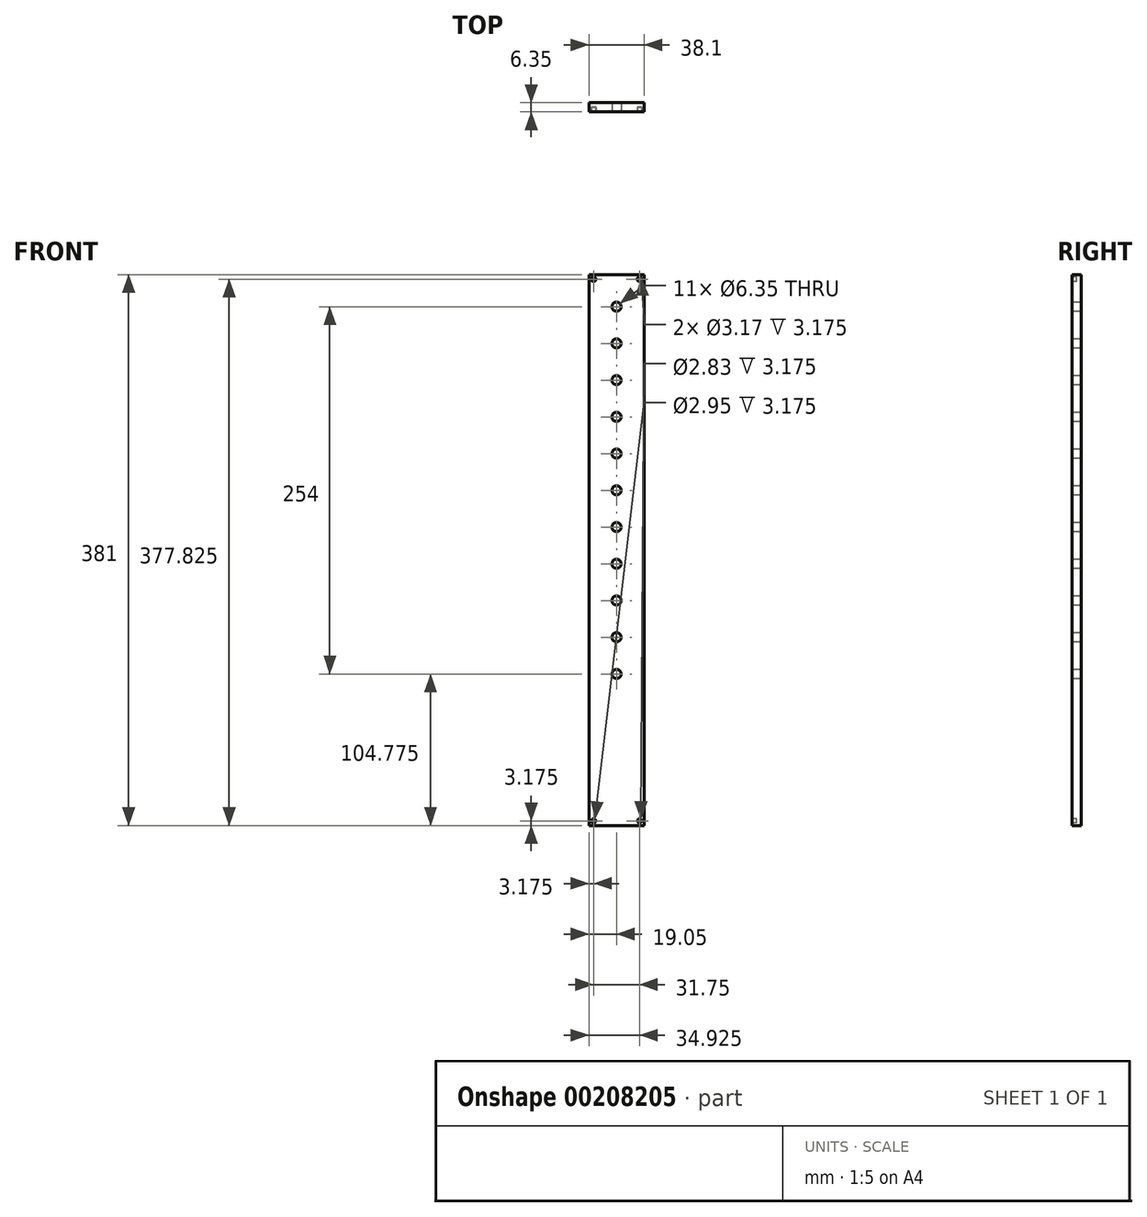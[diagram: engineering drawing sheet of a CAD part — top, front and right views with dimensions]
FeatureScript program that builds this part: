
annotation { "Feature Type Name" : "Feature", "Feature Type Description" : "" }
export const myFeature = defineFeature(function(context is Context, id is Id, definition is map)
    precondition{}
    {
        {
            var Q0;
            Q0=qCreatedBy(makeId("Front.planeOp"),FACE);
            var sketch = newSketch(context, id + "F0", { "sketchPlane" : qUnion([Q0])});
            skLineSegment(sketch, "E0.bottom", {"start": v(-19.05, 190.5) * mm, "end": v(19.05, 190.5) * mm});
            skLineSegment(sketch, "E0.top", {"start": v(-19.05, -190.5) * mm, "end": v(19.05, -190.5) * mm});
            skLineSegment(sketch, "E0.left", {"start": v(-19.05, 190.5) * mm, "end": v(-19.05, -190.5) * mm});
            skLineSegment(sketch, "E0.right", {"start": v(19.05, 190.5) * mm, "end": v(19.05, -190.5) * mm});
            skPoint(sketch, "E0.middle", {"position": v(0, 0) * mm});
            skSolve(sketch);
        }
        {
            var Q0;
            Q0 = qSketchRegion(id + "F0", true);
            extrude(context, id + "F1", {"entities" : qUnion([Q0]), "depth" : 6.35 * mm});
        }
        {
            var Q0;
            Q0=makeQuery(id+"F1.opExtrude","CAP_FACE",FACE,{"disambiguationData":[OSD([sQuery(id+"F0.wireOp",EDGE,"E0.bottom"),sQuery(id+"F0.wireOp",EDGE,"E0.top"),sQuery(id+"F0.wireOp",EDGE,"E0.left"),sQuery(id+"F0.wireOp",EDGE,"E0.right")])],"isStart":false});
            var sketch = newSketch(context, id + "F2", { "sketchPlane" : qUnion([Q0])});
            skLineSegment(sketch, "E1", {"start": v(0, -190.5) * mm, "end": v(0, -88.9) * mm, "construction": true});
            skPoint(sketch, "E1.endSnap0", {"position": v(0, -190.5) * mm});
            skLineSegment(sketch, "E2", {"start": v(0, -88.9) * mm, "end": v(0, -82.55) * mm, "construction": true});
            skCircle(sketch, "E3", {"center": v(0, -85.73) * mm, "radius": 3.18 * mm});
            skLineSegment(sketch, "E4", {"start": v(0, -85.73) * mm, "end": v(0, -60.33) * mm, "construction": true});
            skLineSegment(sketch, "E5", {"start": v(0, -60.33) * mm, "end": v(0, -34.93) * mm, "construction": true});
            skLineSegment(sketch, "E6", {"start": v(0, -34.93) * mm, "end": v(0, -9.53) * mm, "construction": true});
            skLineSegment(sketch, "E7", {"start": v(0, -9.53) * mm, "end": v(0, 15.87) * mm, "construction": true});
            skLineSegment(sketch, "E8", {"start": v(0, 15.87) * mm, "end": v(0, 41.27) * mm, "construction": true});
            skLineSegment(sketch, "E9", {"start": v(0, 41.27) * mm, "end": v(0, 66.67) * mm, "construction": true});
            skLineSegment(sketch, "E10", {"start": v(0, 66.67) * mm, "end": v(0, 92.08) * mm, "construction": true});
            skLineSegment(sketch, "E11", {"start": v(0, 92.08) * mm, "end": v(0, 117.48) * mm, "construction": true});
            skLineSegment(sketch, "E12", {"start": v(0, 117.48) * mm, "end": v(0, 142.88) * mm, "construction": true});
            skLineSegment(sketch, "E13", {"start": v(0, 142.88) * mm, "end": v(0, 168.28) * mm, "construction": true});
            skLineSegment(sketch, "E14", {"start": v(0, 168.28) * mm, "end": v(0, 193.68) * mm, "construction": true});
            skCircle(sketch, "E15", {"center": v(0, -60.33) * mm, "radius": 3.18 * mm});
            skCircle(sketch, "E16", {"center": v(0, -34.93) * mm, "radius": 3.18 * mm});
            skCircle(sketch, "E17", {"center": v(0, -9.53) * mm, "radius": 3.18 * mm});
            skCircle(sketch, "E18", {"center": v(0, 15.87) * mm, "radius": 3.18 * mm});
            skCircle(sketch, "E19", {"center": v(0, 41.27) * mm, "radius": 3.18 * mm});
            skCircle(sketch, "E20", {"center": v(0, 66.67) * mm, "radius": 3.18 * mm});
            skCircle(sketch, "E21", {"center": v(0, 92.08) * mm, "radius": 3.18 * mm});
            skCircle(sketch, "E22", {"center": v(0, 117.48) * mm, "radius": 3.18 * mm});
            skCircle(sketch, "E23", {"center": v(0, 142.88) * mm, "radius": 3.18 * mm});
            skCircle(sketch, "E24", {"center": v(0, 168.28) * mm, "radius": 3.18 * mm});
            skSolve(sketch);
        }
        {
            var Q0;
            Q0 = qSketchRegion(id + "F2", true);
            extrude(context, id + "F3", {"entities" : qUnion([Q0]), "operationType" : NewBodyOperationType.REMOVE, "endBound" : BoundingType.THROUGH_ALL, "oppositeDirection" : true, "depth" : 25.4 * mm});
        }
        {
            var Q0;
            Q0=makeQuery(id+"F1.opExtrude","CAP_FACE",FACE,{"disambiguationData":[OSD([sQuery(id+"F0.wireOp",EDGE,"E0.bottom"),sQuery(id+"F0.wireOp",EDGE,"E0.top"),sQuery(id+"F0.wireOp",EDGE,"E0.left"),sQuery(id+"F0.wireOp",EDGE,"E0.right")])],"isStart":false});
            var sketch = newSketch(context, id + "F4", { "sketchPlane" : qUnion([Q0])});
            skLineSegment(sketch, "E25", {"start": v(-15.88, 187.33) * mm, "end": v(15.88, 187.33) * mm, "construction": true});
            skCircle(sketch, "E26", {"center": v(-15.88, 187.33) * mm, "radius": 1.59 * mm});
            skCircle(sketch, "E27", {"center": v(15.88, 187.33) * mm, "radius": 1.59 * mm});
            skSolve(sketch);
        }
        {
            var Q0;
            Q0 = qSketchRegion(id + "F4", true);
            extrude(context, id + "F5", {"entities" : qUnion([Q0]), "operationType" : NewBodyOperationType.REMOVE, "oppositeDirection" : true, "depth" : 3.17 * mm});
        }
        {
            var Q0;
            Q0=makeQuery(id+"F1.opExtrude","CAP_FACE",FACE,{"disambiguationData":[OSD([sQuery(id+"F0.wireOp",EDGE,"E0.bottom"),sQuery(id+"F0.wireOp",EDGE,"E0.top"),sQuery(id+"F0.wireOp",EDGE,"E0.left"),sQuery(id+"F0.wireOp",EDGE,"E0.right")])],"isStart":false});
            var sketch = newSketch(context, id + "F6", { "sketchPlane" : qUnion([Q0])});
            skLineSegment(sketch, "E28", {"start": v(-15.88, -187.33) * mm, "end": v(15.88, -187.33) * mm, "construction": true});
            skCircle(sketch, "E29", {"center": v(-15.88, -187.33) * mm, "radius": 1.47 * mm});
            skCircle(sketch, "E30", {"center": v(15.88, -187.33) * mm, "radius": 1.41 * mm});
            skSolve(sketch);
        }
        {
            var Q0;
            Q0 = qSketchRegion(id + "F6", true);
            extrude(context, id + "F7", {"entities" : qUnion([Q0]), "operationType" : NewBodyOperationType.REMOVE, "oppositeDirection" : true, "depth" : 3.17 * mm});
        }
    });
